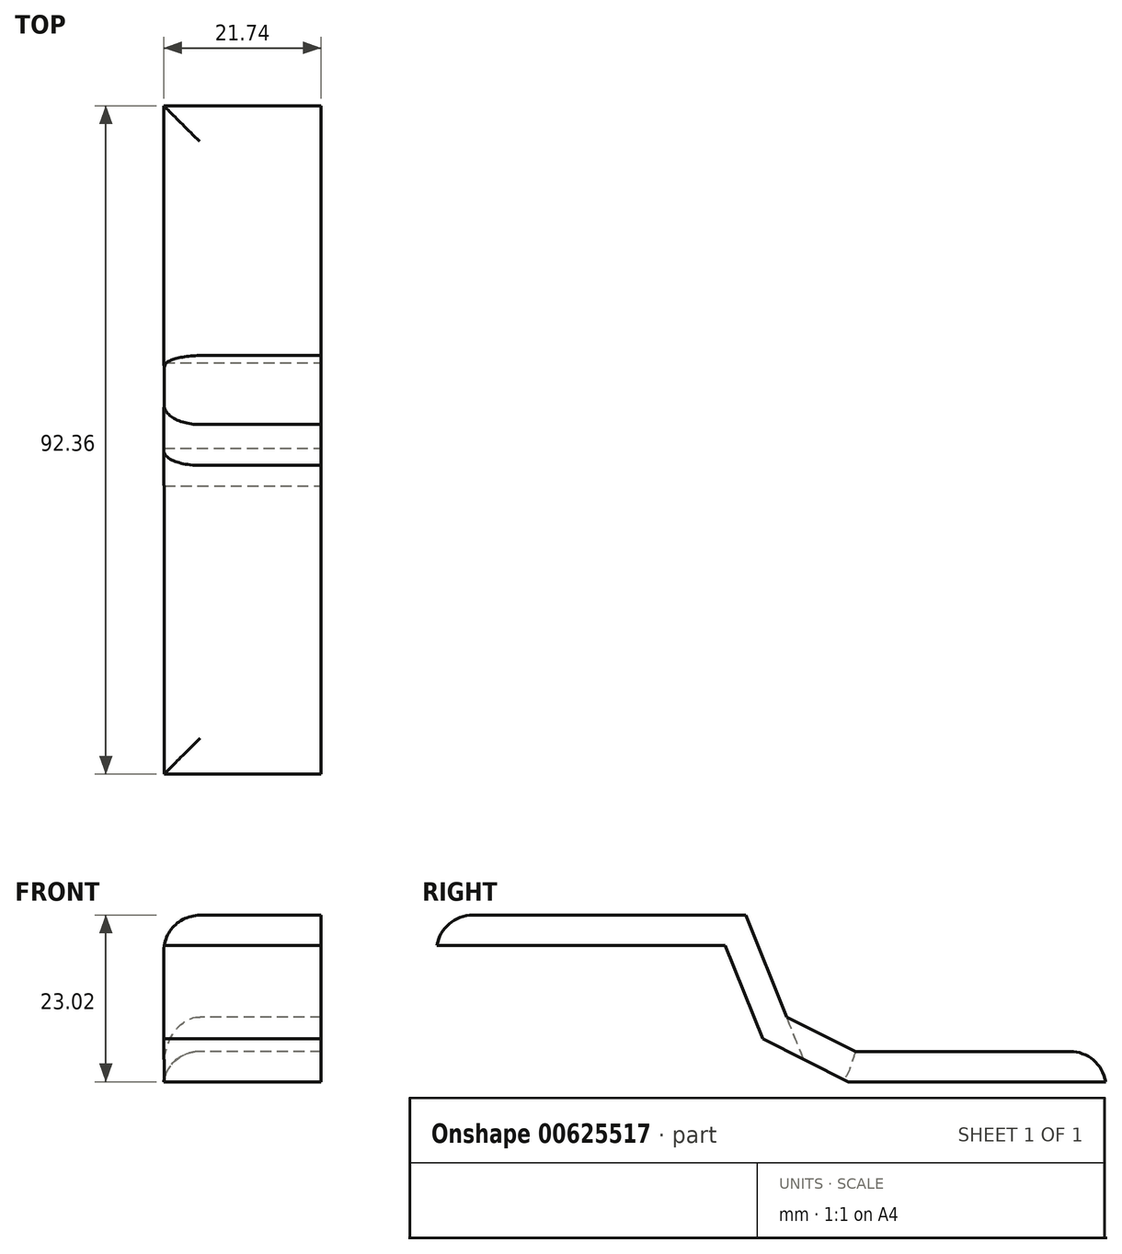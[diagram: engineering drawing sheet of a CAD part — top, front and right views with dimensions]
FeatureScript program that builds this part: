
annotation { "Feature Type Name" : "Feature", "Feature Type Description" : "" }
export const myFeature = defineFeature(function(context is Context, id is Id, definition is map)
    precondition{}
    {
        {
            var Q0;
            Q0=qCreatedBy(makeId("Front.planeOp"),FACE);
            var sketch = newSketch(context, id + "F0", { "sketchPlane" : qUnion([Q0])});
            skLineSegment(sketch, "E0.bottom", {"start": v(-21.74, 4.2) * mm, "end": v(0, 4.2) * mm});
            skLineSegment(sketch, "E0.top", {"start": v(-21.74, 0) * mm, "end": v(0, 0) * mm});
            skLineSegment(sketch, "E0.left", {"start": v(-21.74, 4.2) * mm, "end": v(-21.74, 0) * mm});
            skLineSegment(sketch, "E0.right", {"start": v(0, 4.2) * mm, "end": v(0, 0) * mm});
            skSolve(sketch);
        }
        {
            var Q0;
            Q0=qCreatedBy(makeId("Right.planeOp"),FACE);
            var sketch = newSketch(context, id + "F1", { "sketchPlane" : qUnion([Q0])});
            skLineSegment(sketch, "E1", {"start": v(0, 0) * mm, "end": v(21.25, 0) * mm});
            skLineSegment(sketch, "E2", {"start": v(21.25, 0) * mm, "end": v(39.82, 0) * mm});
            skLineSegment(sketch, "E3", {"start": v(39.82, 0) * mm, "end": v(45, -12.9) * mm});
            skLineSegment(sketch, "E4", {"start": v(45, -12.9) * mm, "end": v(56.84, -18.82) * mm});
            skLineSegment(sketch, "E5", {"start": v(92.36, -18.82) * mm, "end": v(56.84, -18.82) * mm});
            skSolve(sketch);
        }
        {
            var Q0;
            Q0=makeQuery(id+"F0.imprint","IMPRINT",FACE,{"disambiguationData":[TD([[makeQuery(id+"F0.imprint","IMPRINT",EDGE,{"derivedFrom":sQuery(id+"F0.wireOp",EDGE,"E0.bottom")}),-1.0]])]});
            var Q1;
            Q1=sQuery(id+"F1.wireOp",EDGE,"E5");
            var Q2;
            Q2=sQuery(id+"F1.wireOp",EDGE,"E3");
            var Q3;
            Q3=sQuery(id+"F1.wireOp",EDGE,"E4");
            var Q4;
            Q4=sQuery(id+"F1.wireOp",EDGE,"E2");
            var Q5;
            Q5=sQuery(id+"F1.wireOp",EDGE,"E1");
            sweep(context, id + "F2", {"profiles" : qUnion([Q0]), "path" : qUnion([Q1, Q2, Q3, Q4, Q5])});
        }
        {
            var Q0;
            Q0=makeQuery(id+"F2.opSweep","CAP_EDGE",EDGE,{"disambiguationData":[OSD([sQuery(id+"F0.wireOp",EDGE,"E0.bottom"),sQuery(id+"F1.wireOp",VERTEX,"E5.end")])],"isStart":false});
            var Q1;
            Q1=makeQuery(id+"F2.opSweep","SWEPT_EDGE",EDGE,{"disambiguationData":[OSD([sQuery(id+"F0.wireOp",EDGE,"E0.bottom"),sQuery(id+"F0.wireOp",EDGE,"E0.left"),sQuery(id+"F1.wireOp",EDGE,"E5")])]});
            var Q2;
            Q2=makeQuery(id+"F2.opSweep","SWEPT_EDGE",EDGE,{"disambiguationData":[OSD([sQuery(id+"F0.wireOp",EDGE,"E0.bottom"),sQuery(id+"F0.wireOp",EDGE,"E0.left"),sQuery(id+"F1.wireOp",EDGE,"E4")])]});
            var Q3;
            Q3=makeQuery(id+"F2.opSweep","SWEPT_EDGE",EDGE,{"disambiguationData":[OSD([sQuery(id+"F0.wireOp",EDGE,"E0.bottom"),sQuery(id+"F0.wireOp",EDGE,"E0.left"),sQuery(id+"F1.wireOp",EDGE,"E1")])]});
            var Q4;
            Q4=makeQuery(id+"F2.opSweep","CAP_EDGE",EDGE,{"disambiguationData":[OSD([sQuery(id+"F0.wireOp",EDGE,"E0.bottom"),sQuery(id+"F1.wireOp",VERTEX,"E1.start")])],"isStart":true});
            fillet(context, id + "F3", {"entities" : qUnion([Q0, Q1, Q2, Q3, Q4]), "radius" : 5 * mm, "tangentPropagation" : true, "allowEdgeOverflow" : false});
        }
    });
